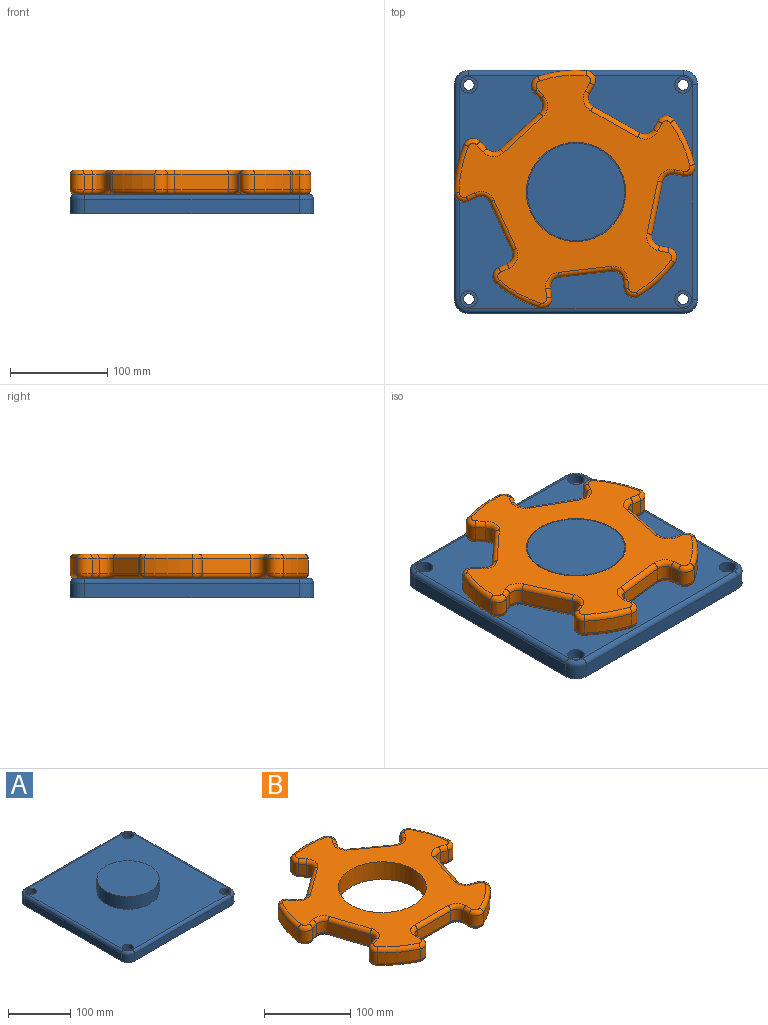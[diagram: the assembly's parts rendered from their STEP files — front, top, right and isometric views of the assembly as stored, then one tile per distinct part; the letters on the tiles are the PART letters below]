
ASSEMBLY  parts=2 mates=1
PART A: 32 faces, bbox 252.5x252.5x45 mm
  f0: plane 220x15mm, normal (1,0,0), area 3300mm2, adj f5,f8,f11,f27
  f1: plane 220x15mm, normal (0,1,0), area 3300mm2, adj f5,f8,f9,f31
  f2: plane 220x15mm, normal (-1,0,0), area 3300mm2, adj f5,f9,f10,f28
  f3: plane 220x15mm, normal (0,-1,0), area 3300mm2, adj f5,f10,f11,f24
  f4: plane 240x240mm, normal (0,0,1), area 48725.4mm2, adj f6,f14,f17,f20,f23,f24,f25,f26
  f5: plane 250x250mm, normal (0,0,-1), area 61926.7mm2, adj f0,f1,f2,f3,f8,f9,f10,f11
  f6: cylinder r=50mm len=100mm, axis (0,0,-1), area 7854mm2, adj f4,f7
  f7: plane 100x100mm, normal (0,0,1), area 7854mm2, adj f6
  f8: cylinder r=15mm len=15mm, axis (0,0,-1), area 353.4mm2, adj f0,f1,f5,f29
  f9: cylinder r=15mm len=15mm, axis (0,0,1), area 353.4mm2, adj f1,f2,f5,f30
  f10: cylinder r=15mm len=15mm, axis (0,0,-1), area 353.4mm2, adj f2,f3,f5,f26
  f11: cylinder r=15mm len=15mm, axis (0,0,1), area 353.4mm2, adj f0,f3,f5,f25
  f12: cylinder r=5.5mm len=11mm, axis (0,0,1), area 345.6mm2, adj f5,f13
  f13: plane 17.25x17.25mm, normal (0,0,1), area 138.7mm2, adj f12,f14
  f14: cylinder r=8.62mm len=17.25mm, axis (0,0,1), area 541.9mm2, adj f4,f13
  f15: cylinder r=5.5mm len=11mm, axis (0,0,1), area 345.6mm2, adj f5,f16
  f16: plane 17.25x17.25mm, normal (0,0,1), area 138.7mm2, adj f15,f17
  f17: cylinder r=8.62mm len=17.25mm, axis (0,0,1), area 541.9mm2, adj f4,f16
  f18: cylinder r=5.5mm len=11mm, axis (0,0,1), area 345.6mm2, adj f5,f19
  f19: plane 17.25x17.25mm, normal (0,0,1), area 138.7mm2, adj f18,f20
  f20: cylinder r=8.62mm len=17.25mm, axis (0,0,1), area 541.9mm2, adj f4,f19
  f21: cylinder r=5.5mm len=11mm, axis (0,0,1), area 345.6mm2, adj f5,f22
  f22: plane 17.25x17.25mm, normal (0,0,1), area 138.7mm2, adj f21,f23
  f23: cylinder r=8.62mm len=17.25mm, axis (0,0,1), area 541.9mm2, adj f4,f22
  f24: cylinder r=5mm len=220mm, axis (-1,0,0), area 1727.9mm2, adj f3,f4,f25,f26
  f25: torus R=10mm, axis (0,0,1), area 162.6mm2, adj f4,f11,f24,f27
  f26: torus R=10mm, axis (0,0,1), area 162.6mm2, adj f4,f10,f24,f28
  f27: cylinder r=5mm len=220mm, axis (0,-1,0), area 1727.9mm2, adj f0,f4,f25,f29
  f28: cylinder r=5mm len=220mm, axis (0,1,0), area 1727.9mm2, adj f2,f4,f26,f30
  f29: torus R=10mm, axis (0,0,1), area 162.6mm2, adj f4,f8,f27,f31
  f30: torus R=10mm, axis (0,0,1), area 162.6mm2, adj f4,f9,f28,f31
  f31: cylinder r=5mm len=220mm, axis (1,0,0), area 1727.9mm2, adj f1,f4,f29,f30
PART B: 123 faces, bbox 268.9x258.5x25 mm
  f0: plane 238.57x229.73mm, normal (0,0,1), area 21505.7mm2, adj f6,f43,f44,f45,f46,f47,f48,f49
  f1: plane 238.57x229.73mm, normal (0,0,-1), area 21505.7mm2, adj f6,f83,f84,f85,f86,f87,f88,f89
  f2: cylinder r=125mm len=40.68mm, axis (0,0,-1), area 759.5mm2, adj f13,f42,f51,f91
  f3: cylinder r=125mm len=47.82mm, axis (0,0,-1), area 759.5mm2, adj f35,f41,f67,f107
  f4: cylinder r=125mm len=50.29mm, axis (0,0,-1), area 759.5mm2, adj f28,f34,f82,f122
  f5: cylinder r=125mm len=47.82mm, axis (0,0,-1), area 759.5mm2, adj f21,f27,f66,f106
  f6: cylinder r=51mm len=102mm, axis (0,0,-1), area 8011.1mm2, adj f0,f1
  f7: cylinder r=125mm len=40.68mm, axis (0,0,-1), area 759.5mm2, adj f14,f20,f50,f90
  f8: plane 15x9.73mm, normal (-1,0,0), area 146mm2, adj f11,f14,f46,f86
  f9: plane 55x15mm, normal (0,-1,0), area 825mm2, adj f11,f12,f43,f83
  f10: plane 15x9.73mm, normal (1,0,0), area 146mm2, adj f12,f13,f47,f87
  f11: cylinder r=10mm len=15mm, axis (0,0,-1), area 235.6mm2, adj f8,f9,f44,f84
  f12: cylinder r=10mm len=15mm, axis (0,0,-1), area 235.6mm2, adj f9,f10,f45,f85
  f13: cylinder r=10mm len=15mm, axis (0,0,-1), area 299.5mm2, adj f2,f10,f49,f89
  f14: cylinder r=10mm len=15mm, axis (0,0,-1), area 299.5mm2, adj f7,f8,f48,f88
  f15: plane 15x9.26mm, normal (-0.31,-0.95,0), area 146mm2, adj f18,f21,f62,f102
  f16: plane 52.31x17mm, normal (0.95,-0.31,0), area 825mm2, adj f18,f19,f58,f98
  f17: plane 15x9.26mm, normal (0.31,0.95,0), area 146mm2, adj f19,f20,f54,f94
  f18: cylinder r=10mm len=15mm, axis (0,0,-1), area 235.6mm2, adj f15,f16,f60,f100
  f19: cylinder r=10mm len=15mm, axis (0,0,-1), area 235.6mm2, adj f16,f17,f56,f96
  f20: cylinder r=10mm len=16.25mm, axis (0,0,-1), area 299.5mm2, adj f7,f17,f52,f92
  f21: cylinder r=10mm len=15mm, axis (0,0,-1), area 299.5mm2, adj f5,f15,f64,f104
  f22: plane 15x7.87mm, normal (0.81,-0.59,0), area 146mm2, adj f25,f28,f78,f118
  f23: plane 44.5x32.33mm, normal (0.59,0.81,0), area 825mm2, adj f25,f26,f74,f114
  f24: plane 15x7.87mm, normal (-0.81,0.59,0), area 146mm2, adj f26,f27,f70,f110
  f25: cylinder r=10mm len=15mm, axis (0,0,-1), area 235.6mm2, adj f22,f23,f76,f116
  f26: cylinder r=10mm len=15mm, axis (0,0,-1), area 235.6mm2, adj f23,f24,f72,f112
  f27: cylinder r=10mm len=16.78mm, axis (0,0,-1), area 299.5mm2, adj f5,f24,f68,f108
  f28: cylinder r=10mm len=15.67mm, axis (0,0,-1), area 299.5mm2, adj f4,f22,f80,f120
  f29: plane 15x7.87mm, normal (0.81,0.59,0), area 146mm2, adj f32,f35,f71,f111
  f30: plane 44.5x32.33mm, normal (-0.59,0.81,0), area 825mm2, adj f32,f33,f75,f115
  f31: plane 15x7.87mm, normal (-0.81,-0.59,0), area 146mm2, adj f33,f34,f79,f119
  f32: cylinder r=10mm len=15mm, axis (0,0,-1), area 235.6mm2, adj f29,f30,f73,f113
  f33: cylinder r=10mm len=15mm, axis (0,0,-1), area 235.6mm2, adj f30,f31,f77,f117
  f34: cylinder r=10mm len=15.67mm, axis (0,0,-1), area 299.5mm2, adj f4,f31,f81,f121
  f35: cylinder r=10mm len=16.78mm, axis (0,0,-1), area 299.5mm2, adj f3,f29,f69,f109
  f36: plane 15x9.26mm, normal (-0.31,0.95,0), area 146mm2, adj f39,f42,f55,f95
  f37: plane 52.31x17mm, normal (-0.95,-0.31,0), area 825mm2, adj f39,f40,f59,f99
  f38: plane 15x9.26mm, normal (0.31,-0.95,0), area 146mm2, adj f40,f41,f63,f103
  f39: cylinder r=10mm len=15mm, axis (0,0,-1), area 235.6mm2, adj f36,f37,f57,f97
  f40: cylinder r=10mm len=15mm, axis (0,0,-1), area 235.6mm2, adj f37,f38,f61,f101
  f41: cylinder r=10mm len=15mm, axis (0,0,-1), area 299.5mm2, adj f3,f38,f65,f105
  f42: cylinder r=10mm len=16.25mm, axis (0,0,-1), area 299.5mm2, adj f2,f36,f53,f93
  f43: cylinder r=5mm len=55mm, axis (1,0,0), area 432mm2, adj f0,f9,f44,f45
  f44: torus R=15mm, axis (0,0,1), area 145.8mm2, adj f0,f11,f43,f46
  f45: torus R=15mm, axis (0,0,1), area 145.8mm2, adj f0,f12,f43,f47
  f46: cylinder r=5mm len=9.73mm, axis (0,-1,0), area 76.4mm2, adj f0,f8,f44,f48
  f47: cylinder r=5mm len=9.73mm, axis (0,1,0), area 76.4mm2, adj f0,f10,f45,f49
  f48: torus R=5mm, axis (0,0,1), area 128.3mm2, adj f0,f14,f46,f50
  f49: torus R=5mm, axis (0,0,1), area 128.3mm2, adj f0,f13,f47,f51
  f50: torus R=120mm, axis (0,0,1), area 391.9mm2, adj f0,f7,f48,f52
  f51: torus R=120mm, axis (0,0,1), area 391.9mm2, adj f0,f2,f49,f53
  f52: torus R=5mm, axis (0,0,1), area 128.3mm2, adj f0,f20,f50,f54
  f53: torus R=5mm, axis (0,0,1), area 128.3mm2, adj f0,f42,f51,f55
  f54: cylinder r=5mm len=10.8mm, axis (-0.95,0.31,0), area 76.4mm2, adj f0,f17,f52,f56
  f55: cylinder r=5mm len=10.8mm, axis (-0.95,-0.31,0), area 76.4mm2, adj f0,f36,f53,f57
  f56: torus R=15mm, axis (0,0,1), area 145.8mm2, adj f0,f19,f54,f58
  f57: torus R=15mm, axis (0,0,1), area 145.8mm2, adj f0,f39,f55,f59
  f58: cylinder r=5mm len=53.85mm, axis (0.31,0.95,0), area 432mm2, adj f0,f16,f56,f60
  f59: cylinder r=5mm len=53.85mm, axis (0.31,-0.95,0), area 432mm2, adj f0,f37,f57,f61
  f60: torus R=15mm, axis (0,0,1), area 145.8mm2, adj f0,f18,f58,f62
  f61: torus R=15mm, axis (0,0,1), area 145.8mm2, adj f0,f40,f59,f63
  f62: cylinder r=5mm len=10.8mm, axis (0.95,-0.31,0), area 76.4mm2, adj f0,f15,f60,f64
  f63: cylinder r=5mm len=10.8mm, axis (0.95,0.31,0), area 76.4mm2, adj f0,f38,f61,f65
  f64: torus R=5mm, axis (0,0,1), area 128.3mm2, adj f0,f21,f62,f66
  f65: torus R=5mm, axis (0,0,1), area 128.3mm2, adj f0,f41,f63,f67
  f66: torus R=120mm, axis (0,0,1), area 391.9mm2, adj f0,f5,f64,f68
  f67: torus R=120mm, axis (0,0,1), area 391.9mm2, adj f0,f3,f65,f69
  f68: torus R=5mm, axis (0,0,1), area 128.3mm2, adj f0,f27,f66,f70
  f69: torus R=5mm, axis (0,0,1), area 128.3mm2, adj f0,f35,f67,f71
  f70: cylinder r=5mm len=10.81mm, axis (-0.59,-0.81,0), area 76.4mm2, adj f0,f24,f68,f72
  f71: cylinder r=5mm len=10.81mm, axis (-0.59,0.81,0), area 76.4mm2, adj f0,f29,f69,f73
  f72: torus R=15mm, axis (0,0,1), area 145.8mm2, adj f0,f26,f70,f74
  f73: torus R=15mm, axis (0,0,1), area 145.8mm2, adj f0,f32,f71,f75
  f74: cylinder r=5mm len=47.44mm, axis (-0.81,0.59,0), area 432mm2, adj f0,f23,f72,f76
  f75: cylinder r=5mm len=47.44mm, axis (-0.81,-0.59,0), area 432mm2, adj f0,f30,f73,f77
  f76: torus R=15mm, axis (0,0,1), area 145.8mm2, adj f0,f25,f74,f78
  f77: torus R=15mm, axis (0,0,1), area 145.8mm2, adj f0,f33,f75,f79
  f78: cylinder r=5mm len=10.81mm, axis (0.59,0.81,0), area 76.4mm2, adj f0,f22,f76,f80
  f79: cylinder r=5mm len=10.81mm, axis (0.59,-0.81,0), area 76.4mm2, adj f0,f31,f77,f81
  f80: torus R=5mm, axis (0,0,1), area 128.3mm2, adj f0,f28,f78,f82
  f81: torus R=5mm, axis (0,0,1), area 128.3mm2, adj f0,f34,f79,f82
  f82: torus R=120mm, axis (0,0,1), area 391.9mm2, adj f0,f4,f80,f81
  f83: cylinder r=5mm len=55mm, axis (-1,0,0), area 432mm2, adj f1,f9,f84,f85
  f84: torus R=15mm, axis (0,0,1), area 145.8mm2, adj f1,f11,f83,f86
  f85: torus R=15mm, axis (0,0,1), area 145.8mm2, adj f1,f12,f83,f87
  f86: cylinder r=5mm len=9.73mm, axis (0,1,0), area 76.4mm2, adj f1,f8,f84,f88
  f87: cylinder r=5mm len=9.73mm, axis (0,-1,0), area 76.4mm2, adj f1,f10,f85,f89
  f88: torus R=5mm, axis (0,0,1), area 128.3mm2, adj f1,f14,f86,f90
  f89: torus R=5mm, axis (0,0,1), area 128.3mm2, adj f1,f13,f87,f91
  f90: torus R=120mm, axis (0,0,1), area 391.9mm2, adj f1,f7,f88,f92
  f91: torus R=120mm, axis (0,0,1), area 391.9mm2, adj f1,f2,f89,f93
  f92: torus R=5mm, axis (0,0,1), area 128.3mm2, adj f1,f20,f90,f94
  f93: torus R=5mm, axis (0,0,1), area 128.3mm2, adj f1,f42,f91,f95
  f94: cylinder r=5mm len=10.8mm, axis (0.95,-0.31,0), area 76.4mm2, adj f1,f17,f92,f96
  f95: cylinder r=5mm len=10.8mm, axis (0.95,0.31,0), area 76.4mm2, adj f1,f36,f93,f97
  f96: torus R=15mm, axis (0,0,1), area 145.8mm2, adj f1,f19,f94,f98
  f97: torus R=15mm, axis (0,0,1), area 145.8mm2, adj f1,f39,f95,f99
  f98: cylinder r=5mm len=53.85mm, axis (-0.31,-0.95,0), area 432mm2, adj f1,f16,f96,f100
  f99: cylinder r=5mm len=53.85mm, axis (-0.31,0.95,0), area 432mm2, adj f1,f37,f97,f101
  f100: torus R=15mm, axis (0,0,1), area 145.8mm2, adj f1,f18,f98,f102
  f101: torus R=15mm, axis (0,0,1), area 145.8mm2, adj f1,f40,f99,f103
  f102: cylinder r=5mm len=10.8mm, axis (-0.95,0.31,0), area 76.4mm2, adj f1,f15,f100,f104
  f103: cylinder r=5mm len=10.8mm, axis (-0.95,-0.31,0), area 76.4mm2, adj f1,f38,f101,f105
  f104: torus R=5mm, axis (0,0,1), area 128.3mm2, adj f1,f21,f102,f106
  f105: torus R=5mm, axis (0,0,1), area 128.3mm2, adj f1,f41,f103,f107
  f106: torus R=120mm, axis (0,0,1), area 391.9mm2, adj f1,f5,f104,f108
  f107: torus R=120mm, axis (0,0,1), area 391.9mm2, adj f1,f3,f105,f109
  f108: torus R=5mm, axis (0,0,1), area 128.3mm2, adj f1,f27,f106,f110
  f109: torus R=5mm, axis (0,0,1), area 128.3mm2, adj f1,f35,f107,f111
  f110: cylinder r=5mm len=10.81mm, axis (0.59,0.81,0), area 76.4mm2, adj f1,f24,f108,f112
  f111: cylinder r=5mm len=10.81mm, axis (0.59,-0.81,0), area 76.4mm2, adj f1,f29,f109,f113
  f112: torus R=15mm, axis (0,0,1), area 145.8mm2, adj f1,f26,f110,f114
  f113: torus R=15mm, axis (0,0,1), area 145.8mm2, adj f1,f32,f111,f115
  f114: cylinder r=5mm len=47.44mm, axis (0.81,-0.59,0), area 432mm2, adj f1,f23,f112,f116
  f115: cylinder r=5mm len=47.44mm, axis (0.81,0.59,0), area 432mm2, adj f1,f30,f113,f117
  f116: torus R=15mm, axis (0,0,1), area 145.8mm2, adj f1,f25,f114,f118
  f117: torus R=15mm, axis (0,0,1), area 145.8mm2, adj f1,f33,f115,f119
  f118: cylinder r=5mm len=10.81mm, axis (-0.59,-0.81,0), area 76.4mm2, adj f1,f22,f116,f120
  f119: cylinder r=5mm len=10.81mm, axis (-0.59,0.81,0), area 76.4mm2, adj f1,f31,f117,f121
  f120: torus R=5mm, axis (0,0,1), area 128.3mm2, adj f1,f28,f118,f122
  f121: torus R=5mm, axis (0,0,1), area 128.3mm2, adj f1,f34,f119,f122
  f122: torus R=120mm, axis (0,0,1), area 391.9mm2, adj f1,f4,f120,f121
PLACE A at identity fixed
PLACE B rot(axis=(0,0,1),150.6deg) t=(0,0,0)mm
MATE revolute B.f2 <-> A.f6  axis (0,0,-1) through (0,0,45)mm
